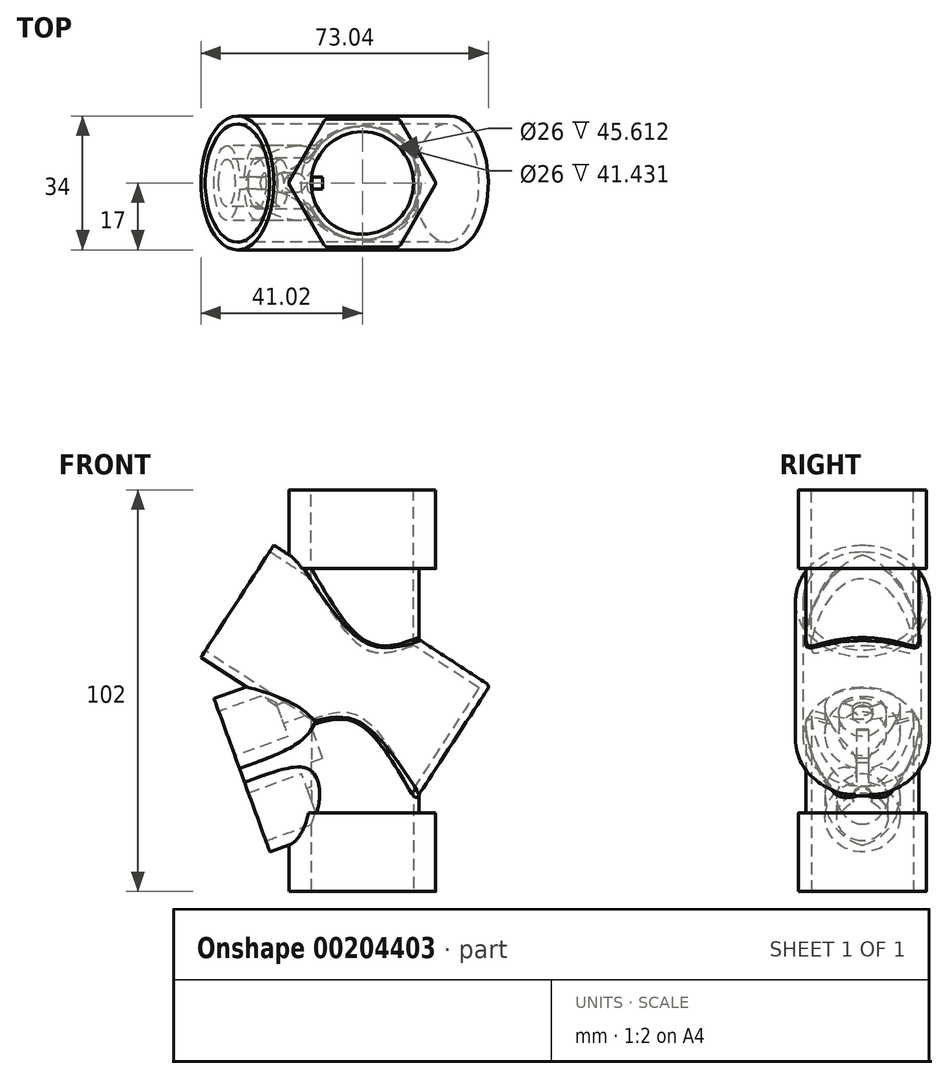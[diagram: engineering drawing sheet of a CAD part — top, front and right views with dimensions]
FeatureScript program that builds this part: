
annotation { "Feature Type Name" : "Feature", "Feature Type Description" : "" }
export const myFeature = defineFeature(function(context is Context, id is Id, definition is map)
    precondition{}
    {
        {
            var Q0;
            Q0=qCreatedBy(makeId("Top.planeOp"),FACE);
            var sketch = newSketch(context, id + "F0", { "sketchPlane" : qUnion([Q0])});
            skCircle(sketch, "E0", {"center": v(0, 0) * mm, "radius": 13 * mm});
            skCircle(sketch, "E1.cCircle", {"center": v(0, 0) * mm, "radius": 16.25 * mm, "construction": true});
            skLineSegment(sketch, "E1.0", {"start": v(8.8, -16.25) * mm, "end": v(-8.8, -16.25) * mm});
            skLineSegment(sketch, "E1.1", {"start": v(-9.67, -15.75) * mm, "end": v(-18.48, -0.5) * mm});
            skLineSegment(sketch, "E1.2", {"start": v(-18.48, 0.5) * mm, "end": v(-9.67, 15.75) * mm});
            skLineSegment(sketch, "E1.3", {"start": v(-8.8, 16.25) * mm, "end": v(8.8, 16.25) * mm});
            skLineSegment(sketch, "E1.4", {"start": v(9.67, 15.75) * mm, "end": v(18.48, 0.5) * mm});
            skLineSegment(sketch, "E1.5", {"start": v(18.48, -0.5) * mm, "end": v(9.67, -15.75) * mm});
            skPoint(sketch, "E1.0.midPoint", {"position": v(0, -16.25) * mm});
            skPoint(sketch, "E2.visualSharp", {"position": v(-18.76, 0) * mm});
            skArc(sketch, "E2.filletArc", {"start": v(-18.48, 0.5) * mm, "mid": v(-18.6, 0) * mm, "end": v(-18.48, -0.5) * mm});
            skPoint(sketch, "E3.visualSharp", {"position": v(-9.38, -16.25) * mm});
            skArc(sketch, "E3.filletArc", {"start": v(-9.67, -15.75) * mm, "mid": v(-9.3, -16.12) * mm, "end": v(-8.8, -16.25) * mm});
            skPoint(sketch, "E4.visualSharp", {"position": v(9.38, -16.25) * mm});
            skArc(sketch, "E4.filletArc", {"start": v(8.8, -16.25) * mm, "mid": v(9.3, -16.12) * mm, "end": v(9.67, -15.75) * mm});
            skPoint(sketch, "E5.visualSharp", {"position": v(18.76, 0) * mm});
            skArc(sketch, "E5.filletArc", {"start": v(18.48, -0.5) * mm, "mid": v(18.6, 0) * mm, "end": v(18.48, 0.5) * mm});
            skPoint(sketch, "E6.visualSharp", {"position": v(9.38, 16.25) * mm});
            skArc(sketch, "E6.filletArc", {"start": v(9.67, 15.75) * mm, "mid": v(9.3, 16.12) * mm, "end": v(8.8, 16.25) * mm});
            skPoint(sketch, "E7.visualSharp", {"position": v(-9.38, 16.25) * mm});
            skArc(sketch, "E7.filletArc", {"start": v(-8.8, 16.25) * mm, "mid": v(-9.3, 16.12) * mm, "end": v(-9.67, 15.75) * mm});
            skSolve(sketch);
        }
        {
            var Q0;
            Q0=makeQuery(id+"F0.imprint","IMPRINT",FACE,{"disambiguationData":[TD([[makeQuery(id+"F0.imprint","IMPRINT",EDGE,{"derivedFrom":sQuery(id+"F0.wireOp",EDGE,"E0")}),-1.0]])]});
            extrude(context, id + "F1", {"entities" : qUnion([Q0]), "depth" : 20 * mm});
        }
        {
            var Q0;
            Q0=makeQuery(id+"F1.opExtrude","CAP_FACE",FACE,{"disambiguationData":[OSD([sQuery(id+"F0.wireOp",EDGE,"E0"),sQuery(id+"F0.wireOp",EDGE,"E1.0"),sQuery(id+"F0.wireOp",EDGE,"E1.1"),sQuery(id+"F0.wireOp",EDGE,"E1.2"),sQuery(id+"F0.wireOp",EDGE,"E1.3"),sQuery(id+"F0.wireOp",EDGE,"E1.4"),sQuery(id+"F0.wireOp",EDGE,"E1.5"),sQuery(id+"F0.wireOp",EDGE,"E2.filletArc"),sQuery(id+"F0.wireOp",EDGE,"E3.filletArc"),sQuery(id+"F0.wireOp",EDGE,"E4.filletArc"),sQuery(id+"F0.wireOp",EDGE,"E5.filletArc"),sQuery(id+"F0.wireOp",EDGE,"E6.filletArc"),sQuery(id+"F0.wireOp",EDGE,"E7.filletArc")])],"isStart":false});
            var sketch = newSketch(context, id + "F2", { "sketchPlane" : qUnion([Q0])});
            skCircle(sketch, "E8", {"center": v(0, 0) * mm, "radius": 14.4 * mm});
            skCircle(sketch, "E9", {"center": v(0, 0) * mm, "radius": 9 * mm});
            skSolve(sketch);
        }
        {
            var Q0;
            Q0=makeQuery(id+"F2.imprint","IMPRINT",FACE,{"disambiguationData":[TD([[makeQuery(id+"F2.imprint","IMPRINT",EDGE,{"derivedFrom":sQuery(id+"F2.wireOp",EDGE,"E8")}),1.0]])]});
            var Q1;
            Q1=makeQuery(id+"F2.imprint","IMPRINT",FACE,{"disambiguationData":[TD([[makeQuery(id+"F2.imprint","IMPRINT",EDGE,{"derivedFrom":sQuery(id+"F2.wireOp",EDGE,"E9")}),-1.0]])]});
            extrude(context, id + "F3", {"entities" : qUnion([Q0, Q1]), "operationType" : NewBodyOperationType.ADD, "depth" : 31 * mm});
        }
        {
            var Q0;
            Q0=makeQuery(id+"F1.opExtrude","SWEPT_BODY",BODY,{"disambiguationData":[OSD([sQuery(id+"F0.wireOp",EDGE,"E0"),sQuery(id+"F0.wireOp",EDGE,"E1.0"),sQuery(id+"F0.wireOp",EDGE,"E1.1"),sQuery(id+"F0.wireOp",EDGE,"E1.2"),sQuery(id+"F0.wireOp",EDGE,"E1.3"),sQuery(id+"F0.wireOp",EDGE,"E1.4"),sQuery(id+"F0.wireOp",EDGE,"E1.5"),sQuery(id+"F0.wireOp",EDGE,"E2.filletArc"),sQuery(id+"F0.wireOp",EDGE,"E3.filletArc"),sQuery(id+"F0.wireOp",EDGE,"E4.filletArc"),sQuery(id+"F0.wireOp",EDGE,"E5.filletArc"),sQuery(id+"F0.wireOp",EDGE,"E6.filletArc"),sQuery(id+"F0.wireOp",EDGE,"E7.filletArc")])]});
            var Q1;
            Q1=makeQuery(id+"F3.opExtrude","CAP_FACE",FACE,{"disambiguationData":[OSD([sQuery(id+"F2.wireOp",EDGE,"E8"),sQuery(id+"F2.wireOp",EDGE,"E9")])],"isStart":false});
            mirror(context, id + "F4", {"operationType" : NewBodyOperationType.ADD, "entities" : qUnion([Q0]), "mirrorPlane" : qUnion([Q1])});
        }
        {
            var Q0;
            Q0=qCreatedBy(makeId("Front.planeOp"),FACE);
            var sketch = newSketch(context, id + "F5", { "sketchPlane" : qUnion([Q0])});
            skLineSegment(sketch, "E10", {"start": v(-22.48, 88) * mm, "end": v(31.56, 52.83) * mm});
            skLineSegment(sketch, "E11", {"start": v(14.4, 82) * mm, "end": v(14.4, 28) * mm, "construction": true});
            skLineSegment(sketch, "E12", {"start": v(-32.33, 74.13) * mm, "end": v(23.13, 38.04) * mm, "construction": true});
            skLineSegment(sketch, "E13", {"start": v(31.85, 51.45) * mm, "end": v(23.13, 38.04) * mm});
            skLineSegment(sketch, "E14", {"start": v(23.13, 38.04) * mm, "end": v(14.4, 24.63) * mm, "construction": true});
            skLineSegment(sketch, "E15", {"start": v(14.4, 24.63) * mm, "end": v(-44.96, 63.26) * mm, "construction": true});
            skLineSegment(sketch, "E16.0", {"start": v(29.63, 51.7) * mm, "end": v(21.45, 39.13) * mm});
            skLineSegment(sketch, "E16.1", {"start": v(-23.57, 86.32) * mm, "end": v(29.63, 51.7) * mm});
            skLineSegment(sketch, "E17", {"start": v(-22.48, 88) * mm, "end": v(-23.57, 86.32) * mm});
            skLineSegment(sketch, "E18", {"start": v(21.45, 39.13) * mm, "end": v(23.13, 38.04) * mm});
            skPoint(sketch, "E19.visualSharp", {"position": v(32.4, 52.29) * mm});
            skLineSegment(sketch, "E20", {"start": v(-23.57, 86.32) * mm, "end": v(-31.75, 73.75) * mm});
            skLineSegment(sketch, "E21", {"start": v(-31.75, 73.75) * mm, "end": v(21.45, 39.13) * mm});
            skArc(sketch, "E22.filletArc", {"start": v(31.85, 51.45) * mm, "mid": v(32, 52.2) * mm, "end": v(31.56, 52.83) * mm});
            skSolve(sketch);
        }
        {
            var Q0;
            Q0=makeQuery(id+"F5.imprint","IMPRINT",FACE,{"disambiguationData":[TD([[makeQuery(id+"F5.imprint","IMPRINT",EDGE,{"derivedFrom":sQuery(id+"F5.wireOp",EDGE,"E10")}),-1.0]])]});
            var Q1;
            Q1=sQuery(id+"F5.wireOp",EDGE,"E12");
            revolve(context, id + "F6", {"entities" : qUnion([Q0]), "axis" : qUnion([Q1]), "revolveType" : RevolveType.FULL});
        }
        {
            var Q0;
            Q0=makeQuery(id+"F5.imprint","IMPRINT",FACE,{"disambiguationData":[TD([[makeQuery(id+"F5.imprint","IMPRINT",EDGE,{"derivedFrom":sQuery(id+"F5.wireOp",EDGE,"E16.0")}),-1.0]])]});
            var Q1;
            Q1=sQuery(id+"F5.wireOp",EDGE,"E21");
            revolve(context, id + "F7", {"operationType" : NewBodyOperationType.REMOVE, "entities" : qUnion([Q0]), "axis" : qUnion([Q1]), "revolveType" : RevolveType.FULL, "oppositeDirection" : true});
        }
        {
            var Q0;
            Q0=makeQuery(id+"F4.opPattern","COPY",FACE,{"derivedFrom":makeQuery(id+"F3.opExtrude","CAP_FACE",FACE,{"disambiguationData":[OSD([sQuery(id+"F2.wireOp",EDGE,"E8"),sQuery(id+"F2.wireOp",EDGE,"E9")])],"isStart":true}),"instanceName":"1"});
            var sketch = newSketch(context, id + "F8", { "sketchPlane" : qUnion([Q0])});
            skCircle(sketch, "E23", {"center": v(0, 0) * mm, "radius": 13 * mm});
            skSolve(sketch);
        }
        {
            var Q0;
            Q0=qSketchRegion(id+"F8",true);
            extrude(context, id + "F9", {"entities" : qUnion([Q0]), "operationType" : NewBodyOperationType.REMOVE, "depth" : 25 * mm});
        }
        {
            var Q0;
            Q0=qSketchRegion(id+"F8",true);
            var Q1;
            Q1=makeQuery(id+"F4.opPattern","COPY",FACE,{"derivedFrom":makeQuery(id+"F3.opExtrude","CAP_FACE",FACE,{"disambiguationData":[OSD([sQuery(id+"F2.wireOp",EDGE,"E8"),sQuery(id+"F2.wireOp",EDGE,"E9")])],"isStart":true}),"instanceName":"1"});
            extrude(context, id + "F10", {"entities" : qUnion([Q0, Q1]), "operationType" : NewBodyOperationType.REMOVE, "oppositeDirection" : true, "depth" : 7 * mm});
        }
        {
            var Q0;
            Q0=makeQuery(id+"F6.opRevolve","SWEPT_BODY",BODY,{"disambiguationData":[OSD([sQuery(id+"F5.wireOp",EDGE,"E10"),sQuery(id+"F5.wireOp",EDGE,"E13"),sQuery(id+"F5.wireOp",EDGE,"E16.0"),sQuery(id+"F5.wireOp",EDGE,"E16.1"),sQuery(id+"F5.wireOp",EDGE,"E17"),sQuery(id+"F5.wireOp",EDGE,"E18"),sQuery(id+"F5.wireOp",EDGE,"E19.filletArc")])]});
            var Q1;
            Q1=makeQuery(id+"F1.opExtrude","SWEPT_BODY",BODY,{"disambiguationData":[OSD([sQuery(id+"F0.wireOp",EDGE,"E0"),sQuery(id+"F0.wireOp",EDGE,"E1.0"),sQuery(id+"F0.wireOp",EDGE,"E1.1"),sQuery(id+"F0.wireOp",EDGE,"E1.2"),sQuery(id+"F0.wireOp",EDGE,"E1.3"),sQuery(id+"F0.wireOp",EDGE,"E1.4"),sQuery(id+"F0.wireOp",EDGE,"E1.5"),sQuery(id+"F0.wireOp",EDGE,"E2.filletArc"),sQuery(id+"F0.wireOp",EDGE,"E3.filletArc"),sQuery(id+"F0.wireOp",EDGE,"E4.filletArc"),sQuery(id+"F0.wireOp",EDGE,"E5.filletArc"),sQuery(id+"F0.wireOp",EDGE,"E6.filletArc"),sQuery(id+"F0.wireOp",EDGE,"E7.filletArc")])]});
            booleanBodies(context, id + "F11", {"operationType" : BooleanOperationType.UNION, "tools" : qUnion([Q0, Q1])});
        }
        {
            var Q0;
            Q0=makeQuery(id+"F4.opPattern","COPY",EDGE,{"derivedFrom":makeQuery(id+"F3.opExtrude","CAP_EDGE",EDGE,{"disambiguationData":[OSD([sQuery(id+"F2.wireOp",EDGE,"E8")])],"isStart":true}),"instanceName":"1"});
            var Q1;
            Q1=makeQuery(id+"F3.opExtrude","CAP_EDGE",EDGE,{"disambiguationData":[OSD([sQuery(id+"F2.wireOp",EDGE,"E8")])],"isStart":true});
            var Q2;
            Q2=makeQuery(id+"F4.opPattern","COPY",EDGE,{"derivedFrom":makeQuery(id+"F3.opExtrude","CAP_EDGE",EDGE,{"disambiguationData":[OSD([sQuery(id+"F2.wireOp",EDGE,"E9")])],"isStart":true}),"instanceName":"1"});
            var Q3;
            Q3=makeQuery(id+"F3.opExtrude","CAP_EDGE",EDGE,{"disambiguationData":[OSD([sQuery(id+"F2.wireOp",EDGE,"E9")])],"isStart":true});
            chamfer(context, id + "F12", {"entities" : qUnion([Q0, Q1, Q2, Q3]), "width" : 7 * mm, "tangentPropagation" : true});
        }
        {
            var Q0;
            Q0=qCreatedBy(makeId("Top.planeOp"),FACE);
            var sketch = newSketch(context, id + "F13", { "sketchPlane" : qUnion([Q0])});
            skCircle(sketch, "E24", {"center": v(0, 0) * mm, "radius": 9 * mm});
            skSolve(sketch);
        }
        {
            var Q0;
            Q0=qSketchRegion(id+"F13",true);
            extrude(context, id + "F14", {"entities" : qUnion([Q0]), "operationType" : NewBodyOperationType.REMOVE, "depth" : 100 * mm});
        }
        {
            var Q0;
            Q0=qCreatedBy(makeId("Front.planeOp"),FACE);
            var sketch = newSketch(context, id + "F15", { "sketchPlane" : qUnion([Q0])});
            skLineSegment(sketch, "E25", {"start": v(0, 90.32) * mm, "end": v(0, -35.6) * mm, "construction": true});
            skLineSegment(sketch, "E26", {"start": v(-32.67, 10) * mm, "end": v(0, 10) * mm, "construction": true});
            skLineSegment(sketch, "E27", {"start": v(-23.48, 10) * mm, "end": v(-35.59, 43.27) * mm, "construction": true});
            skLineSegment(sketch, "E28", {"start": v(-23.48, 10) * mm, "end": v(4, 20) * mm});
            skLineSegment(sketch, "E29", {"start": v(4, 20) * mm, "end": v(2.83, 23.22) * mm});
            skLineSegment(sketch, "E30", {"start": v(-24.5, 12.82) * mm, "end": v(-23.48, 10) * mm});
            skLineSegment(sketch, "E31", {"start": v(-26.72, 18.93) * mm, "end": v(-5.9, 26.5) * mm, "construction": true});
            skLineSegment(sketch, "E32", {"start": v(-31.17, 31.14) * mm, "end": v(0.42, 42.64) * mm});
            skLineSegment(sketch, "E33", {"start": v(-34.42, 40.07) * mm, "end": v(-3.06, 51.48) * mm, "construction": true});
            skLineSegment(sketch, "E34", {"start": v(2.83, 23.22) * mm, "end": v(1.61, 26.58) * mm});
            skLineSegment(sketch, "E35", {"start": v(1.61, 26.58) * mm, "end": v(-12.35, 21.5) * mm});
            skLineSegment(sketch, "E36", {"start": v(-12.35, 21.5) * mm, "end": v(-10.98, 17.74) * mm});
            skLineSegment(sketch, "E37", {"start": v(-10.98, 17.74) * mm, "end": v(-24.5, 12.82) * mm});
            skLineSegment(sketch, "E38", {"start": v(-31.17, 31.14) * mm, "end": v(-32.36, 34.42) * mm});
            skLineSegment(sketch, "E39", {"start": v(-32.36, 34.42) * mm, "end": v(-18.84, 39.34) * mm});
            skLineSegment(sketch, "E40", {"start": v(-18.84, 39.34) * mm, "end": v(-20.04, 42.64) * mm});
            skLineSegment(sketch, "E41", {"start": v(-20.04, 42.64) * mm, "end": v(-11.12, 45.89) * mm});
            skLineSegment(sketch, "E42", {"start": v(-8.16, 10) * mm, "end": v(-26.03, 59.09) * mm, "construction": true});
            skLineSegment(sketch, "E43", {"start": v(-11.12, 45.89) * mm, "end": v(-0.33, 49.82) * mm});
            skLineSegment(sketch, "E44", {"start": v(-0.33, 49.82) * mm, "end": v(2.07, 43.24) * mm});
            skLineSegment(sketch, "E45", {"start": v(2.07, 43.24) * mm, "end": v(0.42, 42.64) * mm});
            skSolve(sketch);
        }
        {
            var Q0;
            Q0=makeQuery(id+"F15.imprint","IMPRINT",FACE,{"disambiguationData":[TD([[makeQuery(id+"F15.imprint","IMPRINT",EDGE,{"derivedFrom":sQuery(id+"F15.wireOp",EDGE,"E28")}),1.0]])]});
            var Q1;
            Q1=sQuery(id+"F15.wireOp",EDGE,"E31");
            revolve(context, id + "F16", {"entities" : qUnion([Q0]), "axis" : qUnion([Q1]), "revolveType" : RevolveType.FULL});
        }
        {
            var Q0;
            Q0=makeQuery(id+"F15.imprint","IMPRINT",FACE,{"disambiguationData":[TD([[makeQuery(id+"F15.imprint","IMPRINT",EDGE,{"derivedFrom":sQuery(id+"F15.wireOp",EDGE,"E32")}),1.0]])]});
            var Q1;
            Q1=sQuery(id+"F15.wireOp",EDGE,"E33");
            revolve(context, id + "F17", {"entities" : qUnion([Q0]), "axis" : qUnion([Q1]), "revolveType" : RevolveType.FULL});
        }
        {
            var Q0;
            Q0=makeQuery(id+"F16.opRevolve","SWEPT_FACE",FACE,{"disambiguationData":[OSD([sQuery(id+"F15.wireOp",EDGE,"E36")])]});
            var sketch = newSketch(context, id + "F18", { "sketchPlane" : qUnion([Q0])});
            skCircle(sketch, "E46", {"center": v(0, 26.93) * mm, "radius": 6.5 * mm});
            skSolve(sketch);
        }
        {
            var Q0;
            Q0=qSketchRegion(id+"F18",true);
            extrude(context, id + "F19", {"entities" : qUnion([Q0]), "operationType" : NewBodyOperationType.REMOVE, "depth" : 25 * mm});
        }
        {
            var Q0;
            Q0=makeQuery(id+"F16.opRevolve","SWEPT_FACE",FACE,{"disambiguationData":[OSD([sQuery(id+"F15.wireOp",EDGE,"E36")])]});
            var sketch = newSketch(context, id + "F20", { "sketchPlane" : qUnion([Q0])});
            skCircle(sketch, "E47", {"center": v(0, 26.93) * mm, "radius": 2.5 * mm});
            skSolve(sketch);
        }
        {
            var Q0;
            Q0=qSketchRegion(id+"F20",true);
            extrude(context, id + "F21", {"entities" : qUnion([Q0]), "operationType" : NewBodyOperationType.REMOVE, "oppositeDirection" : true, "depth" : 25 * mm});
        }
        {
            var Q0;
            Q0=makeQuery(id+"F1.opExtrude","CAP_FACE",FACE,{"disambiguationData":[OSD([sQuery(id+"F0.wireOp",EDGE,"E0"),sQuery(id+"F0.wireOp",EDGE,"E1.0"),sQuery(id+"F0.wireOp",EDGE,"E1.1"),sQuery(id+"F0.wireOp",EDGE,"E1.2"),sQuery(id+"F0.wireOp",EDGE,"E1.3"),sQuery(id+"F0.wireOp",EDGE,"E1.4"),sQuery(id+"F0.wireOp",EDGE,"E1.5"),sQuery(id+"F0.wireOp",EDGE,"E2.filletArc"),sQuery(id+"F0.wireOp",EDGE,"E3.filletArc"),sQuery(id+"F0.wireOp",EDGE,"E4.filletArc"),sQuery(id+"F0.wireOp",EDGE,"E5.filletArc"),sQuery(id+"F0.wireOp",EDGE,"E6.filletArc"),sQuery(id+"F0.wireOp",EDGE,"E7.filletArc")])],"isStart":true});
            var sketch = newSketch(context, id + "F22", { "sketchPlane" : qUnion([Q0])});
            skCircle(sketch, "E48", {"center": v(0, 0) * mm, "radius": 13 * mm});
            skSolve(sketch);
        }
        {
            var Q0;
            Q0=qSketchRegion(id+"F22",true);
            extrude(context, id + "F23", {"entities" : qUnion([Q0]), "operationType" : NewBodyOperationType.REMOVE, "oppositeDirection" : true, "depth" : 100 * mm});
        }
        {
            var Q0;
            Q0=makeQuery(id+"F5.imprint","IMPRINT",FACE,{"disambiguationData":[TD([[makeQuery(id+"F5.imprint","IMPRINT",EDGE,{"derivedFrom":sQuery(id+"F5.wireOp",EDGE,"E16.0")}),-1.0]])]});
            var Q1;
            Q1=sQuery(id+"F5.wireOp",EDGE,"E21");
            revolve(context, id + "F24", {"operationType" : NewBodyOperationType.REMOVE, "entities" : qUnion([Q0]), "axis" : qUnion([Q1]), "revolveType" : RevolveType.FULL, "oppositeDirection" : true});
        }
        {
            var Q0;
            Q0=makeQuery(id+"F17.opRevolve","SWEPT_FACE",FACE,{"disambiguationData":[OSD([sQuery(id+"F15.wireOp",EDGE,"E40")])]});
            var sketch = newSketch(context, id + "F25", { "sketchPlane" : qUnion([Q0])});
            skCircle(sketch, "E49", {"center": v(0, 49.43) * mm, "radius": 2.5 * mm});
            skSolve(sketch);
        }
        {
            var Q0;
            Q0=qSketchRegion(id+"F25",true);
            extrude(context, id + "F26", {"entities" : qUnion([Q0]), "operationType" : NewBodyOperationType.REMOVE, "oppositeDirection" : true, "depth" : 25 * mm});
        }
        {
            var Q0;
            Q0=makeQuery(id+"F17.opRevolve","SWEPT_FACE",FACE,{"disambiguationData":[OSD([sQuery(id+"F15.wireOp",EDGE,"E38")])]});
            var sketch = newSketch(context, id + "F27", { "sketchPlane" : qUnion([Q0])});
            skLineSegment(sketch, "E50.bottom", {"start": v(-1.5, 43.03) * mm, "end": v(1.5, 43.03) * mm});
            skLineSegment(sketch, "E50.top", {"start": v(-1.5, 35.26) * mm, "end": v(1.5, 35.26) * mm});
            skLineSegment(sketch, "E50.left", {"start": v(-1.5, 43.03) * mm, "end": v(-1.5, 35.26) * mm});
            skLineSegment(sketch, "E50.right", {"start": v(1.5, 43.03) * mm, "end": v(1.5, 35.26) * mm});
            skLineSegment(sketch, "E51", {"start": v(-1.5, 39.92) * mm, "end": v(0, 39.92) * mm, "construction": true});
            skLineSegment(sketch, "E52", {"start": v(0, 39.92) * mm, "end": v(1.5, 39.92) * mm, "construction": true});
            skSolve(sketch);
        }
        {
            var Q0;
            Q0=qSketchRegion(id+"F27",true);
            extrude(context, id + "F28", {"entities" : qUnion([Q0]), "operationType" : NewBodyOperationType.ADD, "oppositeDirection" : true, "depth" : 20.7 * mm});
        }
        {
            var Q0;
            {var subQ0=makeQuery(id+"F3.opExtrude","SWEPT_FACE",FACE,{"disambiguationData":[OSD([sQuery(id+"F2.wireOp",EDGE,"E8")])]});Q0=makeQuery(id+"F28.boolean.opBoolean","INTERSECT",EDGE,{"derivedFrom":[makeQuery(id+"F11.opBoolean","SPLIT",FACE,{"disambiguationData":[TD([makeQuery(id+"F6.opRevolve","SWEPT_FACE",FACE,{"disambiguationData":[OSD([sQuery(id+"F5.wireOp",EDGE,"E13")])]})])],"derivedFrom":makeQuery(id+"F4.boolean.opBoolean","MERGE",FACE,{"derivedFrom":[subQ0,makeQuery(id+"F4.opPattern","COPY",FACE,{"derivedFrom":subQ0,"instanceName":"1"})]})}),makeQuery(id+"F28.opExtrude","SWEPT_FACE",FACE,{"disambiguationData":[OSD([sQuery(id+"F27.wireOp",EDGE,"E50.right")])]})]});}
            var Q1;
            {var subQ0=makeQuery(id+"F3.opExtrude","SWEPT_FACE",FACE,{"disambiguationData":[OSD([sQuery(id+"F2.wireOp",EDGE,"E8")])]});Q1=makeQuery(id+"F28.boolean.opBoolean","INTERSECT",EDGE,{"derivedFrom":[makeQuery(id+"F11.opBoolean","SPLIT",FACE,{"disambiguationData":[TD([makeQuery(id+"F6.opRevolve","SWEPT_FACE",FACE,{"disambiguationData":[OSD([sQuery(id+"F5.wireOp",EDGE,"E13")])]})])],"derivedFrom":makeQuery(id+"F4.boolean.opBoolean","MERGE",FACE,{"derivedFrom":[subQ0,makeQuery(id+"F4.opPattern","COPY",FACE,{"derivedFrom":subQ0,"instanceName":"1"})]})}),makeQuery(id+"F28.opExtrude","SWEPT_FACE",FACE,{"disambiguationData":[OSD([sQuery(id+"F27.wireOp",EDGE,"E50.left")])]})]});}
            fillet(context, id + "F29", {"entities" : qUnion([Q0, Q1]), "radius" : 20 * mm, "tangentPropagation" : true, "allowEdgeOverflow" : false});
        }
        {
            var Q0;
            {var subQ0=makeQuery(id+"F3.opExtrude","SWEPT_FACE",FACE,{"disambiguationData":[OSD([sQuery(id+"F2.wireOp",EDGE,"E8")])]});Q0=makeQuery(id+"F11.opBoolean","INTERSECT",EDGE,{"disambiguationData":[OD(0.0)],"derivedFrom":[makeQuery(id+"F4.boolean.opBoolean","MERGE",FACE,{"derivedFrom":[subQ0,makeQuery(id+"F4.opPattern","COPY",FACE,{"derivedFrom":subQ0,"instanceName":"1"})]}),makeQuery(id+"F6.opRevolve","SWEPT_FACE",FACE,{"disambiguationData":[OSD([sQuery(id+"F5.wireOp",EDGE,"E10")])]})]});}
            var Q1;
            {var subQ0=makeQuery(id+"F3.opExtrude","SWEPT_FACE",FACE,{"disambiguationData":[OSD([sQuery(id+"F2.wireOp",EDGE,"E8")])]});Q1=makeQuery(id+"F26.boolean.opBoolean","SPLIT",EDGE,{"disambiguationData":[OD(0.0)],"derivedFrom":makeQuery(id+"F11.opBoolean","INTERSECT",EDGE,{"disambiguationData":[OD(1.0)],"derivedFrom":[makeQuery(id+"F4.boolean.opBoolean","MERGE",FACE,{"derivedFrom":[subQ0,makeQuery(id+"F4.opPattern","COPY",FACE,{"derivedFrom":subQ0,"instanceName":"1"})]}),makeQuery(id+"F6.opRevolve","SWEPT_FACE",FACE,{"disambiguationData":[OSD([sQuery(id+"F5.wireOp",EDGE,"E10")])]})]})});}
            var Q2;
            {var subQ0=makeQuery(id+"F3.opExtrude","SWEPT_FACE",FACE,{"disambiguationData":[OSD([sQuery(id+"F2.wireOp",EDGE,"E8")])]});var subQ1=makeQuery(id+"F11.opBoolean","SPLIT",FACE,{"disambiguationData":[TD([makeQuery(id+"F6.opRevolve","SWEPT_FACE",FACE,{"disambiguationData":[OSD([sQuery(id+"F5.wireOp",EDGE,"E13")])]})])],"derivedFrom":makeQuery(id+"F4.boolean.opBoolean","MERGE",FACE,{"derivedFrom":[subQ0,makeQuery(id+"F4.opPattern","COPY",FACE,{"derivedFrom":subQ0,"instanceName":"1"})]})});Q2=makeQuery(id+"F29.opFillet","BLEND_EDGE",EDGE,{"blendedFrom":[makeQuery(id+"F28.boolean.opBoolean","INTERSECT",EDGE,{"derivedFrom":[subQ1,makeQuery(id+"F28.opExtrude","SWEPT_FACE",FACE,{"disambiguationData":[OSD([sQuery(id+"F27.wireOp",EDGE,"E50.right")])]})]}),subQ1],"blendedInto":[subQ1]});}
            var Q3;
            {var subQ0=makeQuery(id+"F3.opExtrude","SWEPT_FACE",FACE,{"disambiguationData":[OSD([sQuery(id+"F2.wireOp",EDGE,"E8")])]});var subQ1=makeQuery(id+"F11.opBoolean","SPLIT",FACE,{"disambiguationData":[TD([makeQuery(id+"F6.opRevolve","SWEPT_FACE",FACE,{"disambiguationData":[OSD([sQuery(id+"F5.wireOp",EDGE,"E13")])]})])],"derivedFrom":makeQuery(id+"F4.boolean.opBoolean","MERGE",FACE,{"derivedFrom":[subQ0,makeQuery(id+"F4.opPattern","COPY",FACE,{"derivedFrom":subQ0,"instanceName":"1"})]})});Q3=makeQuery(id+"F29.opFillet","BLEND_EDGE",EDGE,{"blendedFrom":[makeQuery(id+"F28.boolean.opBoolean","INTERSECT",EDGE,{"derivedFrom":[subQ1,makeQuery(id+"F28.opExtrude","SWEPT_FACE",FACE,{"disambiguationData":[OSD([sQuery(id+"F27.wireOp",EDGE,"E50.left")])]})]}),subQ1],"blendedInto":[subQ1]});}
            fillet(context, id + "F30", {"entities" : qUnion([Q0, Q1, Q2, Q3]), "radius" : 1 * mm, "tangentPropagation" : true, "allowEdgeOverflow" : false});
        }
    });
